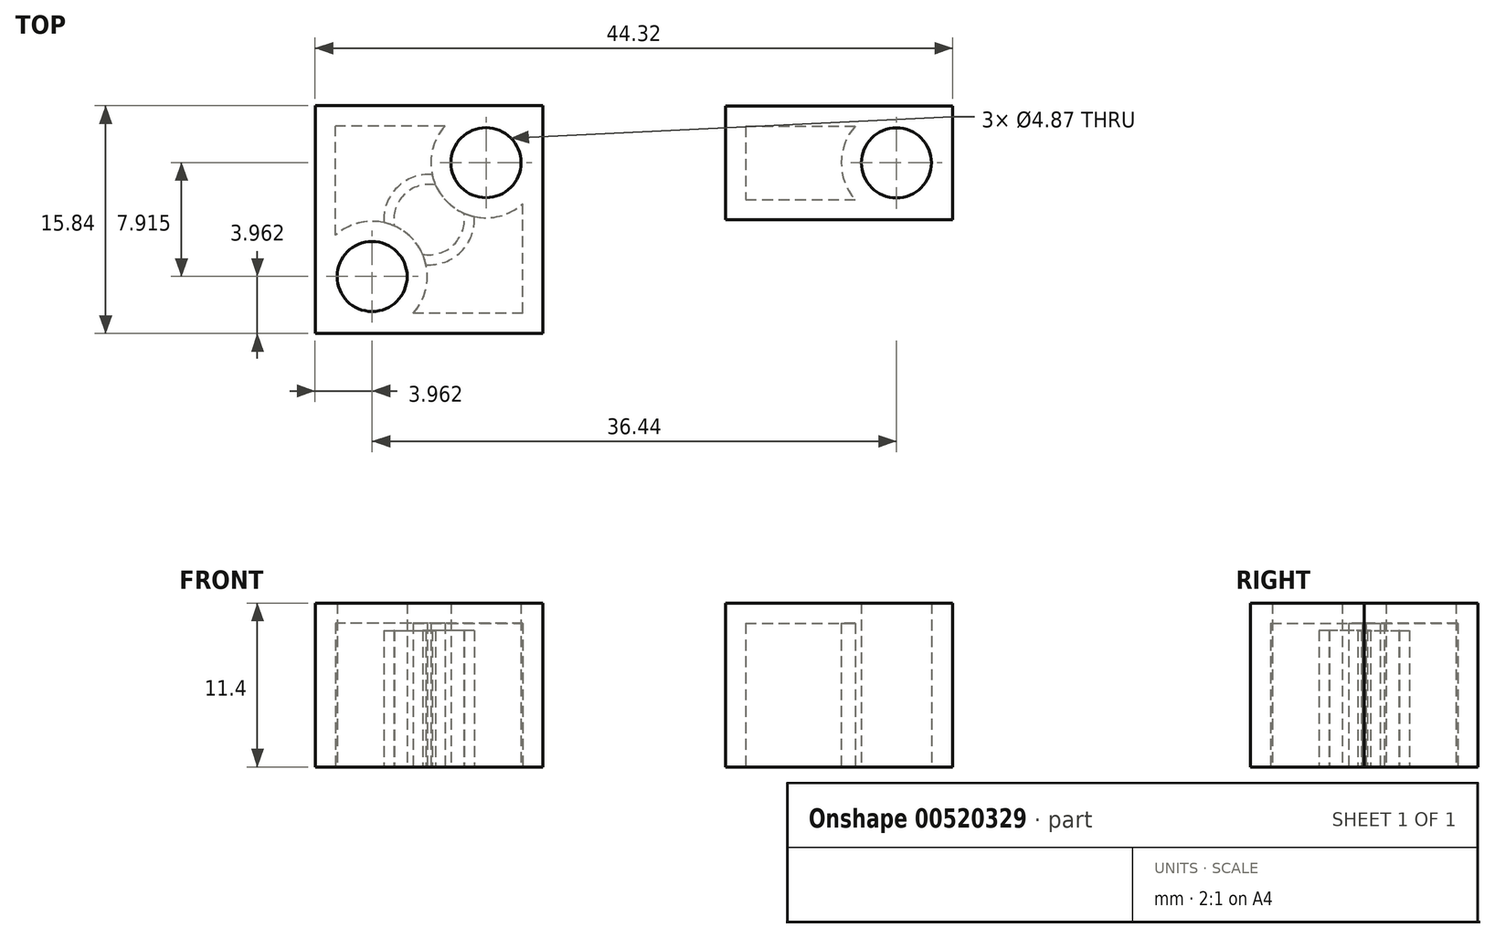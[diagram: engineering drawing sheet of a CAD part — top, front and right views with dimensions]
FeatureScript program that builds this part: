
annotation { "Feature Type Name" : "Feature", "Feature Type Description" : "" }
export const myFeature = defineFeature(function(context is Context, id is Id, definition is map)
    precondition{}
    {
        {
            var Q0;
            Q0=qCreatedBy(makeId("Top.planeOp"),FACE);
            var sketch = newSketch(context, id + "F0", { "sketchPlane" : qUnion([Q0])});
            skLineSegment(sketch, "E0.bottom", {"start": v(7.92, -7.91) * mm, "end": v(-7.91, -7.91) * mm});
            skLineSegment(sketch, "E0.top", {"start": v(7.92, 7.92) * mm, "end": v(-7.91, 7.92) * mm});
            skLineSegment(sketch, "E0.left", {"start": v(7.92, -7.91) * mm, "end": v(7.92, 7.92) * mm});
            skLineSegment(sketch, "E0.right", {"start": v(-7.91, -7.91) * mm, "end": v(-7.91, 7.92) * mm});
            skPoint(sketch, "E0.middle", {"position": v(0, 0) * mm});
            skCircle(sketch, "E1", {"center": v(3.96, -3.96) * mm, "radius": 2.44 * mm});
            skCircle(sketch, "E2.MirrorC", {"center": v(3.96, 3.96) * mm, "radius": 2.44 * mm});
            skCircle(sketch, "E3.MirrorC", {"center": v(-3.96, 3.96) * mm, "radius": 2.44 * mm});
            skCircle(sketch, "E4.MirrorC", {"center": v(-3.96, -3.96) * mm, "radius": 2.44 * mm});
            skLineSegment(sketch, "E5.bottom", {"start": v(20.6, 7.9) * mm, "end": v(36.4, 7.9) * mm});
            skLineSegment(sketch, "E5.left", {"start": v(20.6, 7.9) * mm, "end": v(20.6, 0) * mm});
            skLineSegment(sketch, "E5.right", {"start": v(36.4, 7.9) * mm, "end": v(36.4, 0) * mm});
            skPoint(sketch, "E5.middle", {"position": v(28.5, 0) * mm});
            skLineSegment(sketch, "E6.bottom", {"start": v(20.6, 7.9) * mm, "end": v(22.1, 7.9) * mm});
            skLineSegment(sketch, "E6.left", {"start": v(20.6, 7.9) * mm, "end": v(20.6, 6.4) * mm});
            skLineSegment(sketch, "E7", {"start": v(22.1, 7.9) * mm, "end": v(26.97, 7.9) * mm});
            skLineSegment(sketch, "E8", {"start": v(26.97, 7.9) * mm, "end": v(30.07, 7.9) * mm});
            skLineSegment(sketch, "E9", {"start": v(30.07, 7.9) * mm, "end": v(28.52, 7.9) * mm});
            skCircle(sketch, "E10", {"center": v(24.53, 3.97) * mm, "radius": 2.43 * mm});
            skCircle(sketch, "E11.MirrorC", {"center": v(32.48, 3.94) * mm, "radius": 2.43 * mm});
            skLineSegment(sketch, "E12", {"start": v(20.6, 0) * mm, "end": v(36.4, 0) * mm});
            skPoint(sketch, "E13.orphan", {"position": v(36.4, -7.9) * mm});
            skPoint(sketch, "E14.orphan", {"position": v(20.6, -7.9) * mm});
            skPoint(sketch, "E15.orphan", {"position": v(24.53, 7.9) * mm});
            skPoint(sketch, "E16.orphan", {"position": v(0, 7.92) * mm});
            skPoint(sketch, "E17.end.orphan", {"position": v(0, -7.91) * mm});
            skPoint(sketch, "E18.orphan", {"position": v(-7.91, 0) * mm});
            skPoint(sketch, "E19.start.orphan", {"position": v(7.92, 0) * mm});
            skLineSegment(sketch, "E20", {"start": v(3.96, -3.96) * mm, "end": v(6.4, -3.96) * mm});
            skSolve(sketch);
        }
        {
            var Q0;
            Q0=qSketchRegion(id+"F0",true);
            extrude(context, id + "F1", {"entities" : qUnion([Q0]), "depth" : 9.6 * mm, "offsetDistance" : 25 * mm});
        }
        {
            var Q0;
            Q0=makeQuery(id+"F0.imprint","IMPRINT",FACE,{"disambiguationData":[TD([[makeQuery(id+"F0.imprint","IMPRINT",EDGE,{"derivedFrom":sQuery(id+"F0.wireOp",EDGE,"E3.MirrorC")}),1.0]])]});
            var Q1;
            Q1=makeQuery(id+"F0.imprint","IMPRINT",FACE,{"disambiguationData":[TD([[makeQuery(id+"F0.imprint","IMPRINT",EDGE,{"derivedFrom":sQuery(id+"F0.wireOp",EDGE,"E2.MirrorC")}),-1.0]])]});
            var Q2;
            Q2=makeQuery(id+"F0.imprint","IMPRINT",FACE,{"disambiguationData":[TD([[makeQuery(id+"F0.imprint","IMPRINT",EDGE,{"derivedFrom":sQuery(id+"F0.wireOp",EDGE,"E1")}),1.0]])]});
            var Q3;
            Q3=makeQuery(id+"F0.imprint","IMPRINT",FACE,{"disambiguationData":[TD([[makeQuery(id+"F0.imprint","IMPRINT",EDGE,{"derivedFrom":sQuery(id+"F0.wireOp",EDGE,"E10")}),1.0]])]});
            var Q4;
            Q4=makeQuery(id+"F0.imprint","IMPRINT",FACE,{"disambiguationData":[TD([[makeQuery(id+"F0.imprint","IMPRINT",EDGE,{"derivedFrom":sQuery(id+"F0.wireOp",EDGE,"E11.MirrorC")}),-1.0]])]});
            var Q5;
            Q5=makeQuery(id+"F0.imprint","IMPRINT",FACE,{"disambiguationData":[TD([[makeQuery(id+"F0.imprint","IMPRINT",EDGE,{"derivedFrom":sQuery(id+"F0.wireOp",EDGE,"E4.MirrorC")}),-1.0]])]});
            extrude(context, id + "F2", {"entities" : qUnion([Q0, Q1, Q2, Q3, Q4, Q5]), "operationType" : NewBodyOperationType.ADD, "depth" : 11.4 * mm, "offsetDistance" : 25 * mm});
        }
        {
            var Q0;
            {var subQ0=sQuery(id+"F0.wireOp",EDGE,"E4.MirrorC");var subQ1=sQuery(id+"F0.wireOp",EDGE,"E3.MirrorC");var subQ2=sQuery(id+"F0.wireOp",EDGE,"E2.MirrorC");var subQ3=sQuery(id+"F0.wireOp",EDGE,"E1");Q0=makeQuery(id+"F2.boolean.opBoolean","MERGE",FACE,{"derivedFrom":[makeQuery(id+"F1.opExtrude","CAP_FACE",FACE,{"disambiguationData":[OSD([sQuery(id+"F0.wireOp",EDGE,"E0.bottom"),sQuery(id+"F0.wireOp",EDGE,"E0.top"),sQuery(id+"F0.wireOp",EDGE,"E0.left"),sQuery(id+"F0.wireOp",EDGE,"E0.right"),subQ3,subQ2,subQ1,subQ0])],"isStart":true}),makeQuery(id+"F2.opExtrude","CAP_FACE",FACE,{"disambiguationData":[OSD([subQ3])],"isStart":true}),makeQuery(id+"F2.opExtrude","CAP_FACE",FACE,{"disambiguationData":[OSD([subQ2])],"isStart":true}),makeQuery(id+"F2.opExtrude","CAP_FACE",FACE,{"disambiguationData":[OSD([subQ1])],"isStart":true}),makeQuery(id+"F2.opExtrude","CAP_FACE",FACE,{"disambiguationData":[OSD([subQ0])],"isStart":true})]});}
            var sketch = newSketch(context, id + "F3", { "sketchPlane" : qUnion([Q0])});
            skCircle(sketch, "E21", {"center": v(0, 0) * mm, "radius": 2.45 * mm});
            skCircle(sketch, "E22", {"center": v(0, 0) * mm, "radius": 3.15 * mm});
            skSolve(sketch);
        }
        {
            var Q0;
            {var subQ0=sQuery(id+"F0.wireOp",EDGE,"E4.MirrorC");var subQ1=sQuery(id+"F0.wireOp",EDGE,"E3.MirrorC");var subQ2=sQuery(id+"F0.wireOp",EDGE,"E2.MirrorC");var subQ3=sQuery(id+"F0.wireOp",EDGE,"E1");Q0=makeQuery(id+"F2.boolean.opBoolean","MERGE",FACE,{"derivedFrom":[makeQuery(id+"F1.opExtrude","CAP_FACE",FACE,{"disambiguationData":[OSD([sQuery(id+"F0.wireOp",EDGE,"E0.bottom"),sQuery(id+"F0.wireOp",EDGE,"E0.top"),sQuery(id+"F0.wireOp",EDGE,"E0.left"),sQuery(id+"F0.wireOp",EDGE,"E0.right"),subQ3,subQ2,subQ1,subQ0])],"isStart":true}),makeQuery(id+"F2.opExtrude","CAP_FACE",FACE,{"disambiguationData":[OSD([subQ3])],"isStart":true}),makeQuery(id+"F2.opExtrude","CAP_FACE",FACE,{"disambiguationData":[OSD([subQ2])],"isStart":true}),makeQuery(id+"F2.opExtrude","CAP_FACE",FACE,{"disambiguationData":[OSD([subQ1])],"isStart":true}),makeQuery(id+"F2.opExtrude","CAP_FACE",FACE,{"disambiguationData":[OSD([subQ0])],"isStart":true})]});}
            shell(context, id + "F4", {"entities" : qUnion([Q0]), "thickness" : 1.4 * mm});
        }
        {
            var Q0;
            {var subQ0=sQuery(id+"F0.wireOp",EDGE,"E11.MirrorC");var subQ1=sQuery(id+"F0.wireOp",EDGE,"E10");Q0=makeQuery(id+"F2.boolean.opBoolean","MERGE",FACE,{"derivedFrom":[makeQuery(id+"F1.opExtrude","CAP_FACE",FACE,{"disambiguationData":[OSD([sQuery(id+"F0.wireOp",EDGE,"E5.bottom"),sQuery(id+"F0.wireOp",EDGE,"E5.left"),sQuery(id+"F0.wireOp",EDGE,"E5.right"),sQuery(id+"F0.wireOp",EDGE,"E6.bottom"),sQuery(id+"F0.wireOp",EDGE,"E6.left"),sQuery(id+"F0.wireOp",EDGE,"E7"),sQuery(id+"F0.wireOp",EDGE,"E8"),sQuery(id+"F0.wireOp",EDGE,"E9"),subQ1,subQ0,sQuery(id+"F0.wireOp",EDGE,"E12")])],"isStart":true}),makeQuery(id+"F2.opExtrude","CAP_FACE",FACE,{"disambiguationData":[OSD([subQ1])],"isStart":true}),makeQuery(id+"F2.opExtrude","CAP_FACE",FACE,{"disambiguationData":[OSD([subQ0])],"isStart":true})]});}
            shell(context, id + "F5", {"entities" : qUnion([Q0]), "thickness" : 1.4 * mm});
        }
        {
            var Q0;
            Q0 = qSketchRegion(id + "F3", true);
            extrude(context, id + "F6", {"entities" : qUnion([Q0]), "operationType" : NewBodyOperationType.ADD, "oppositeDirection" : true, "depth" : 9.5 * mm, "offsetDistance" : 25 * mm});
        }
    });
